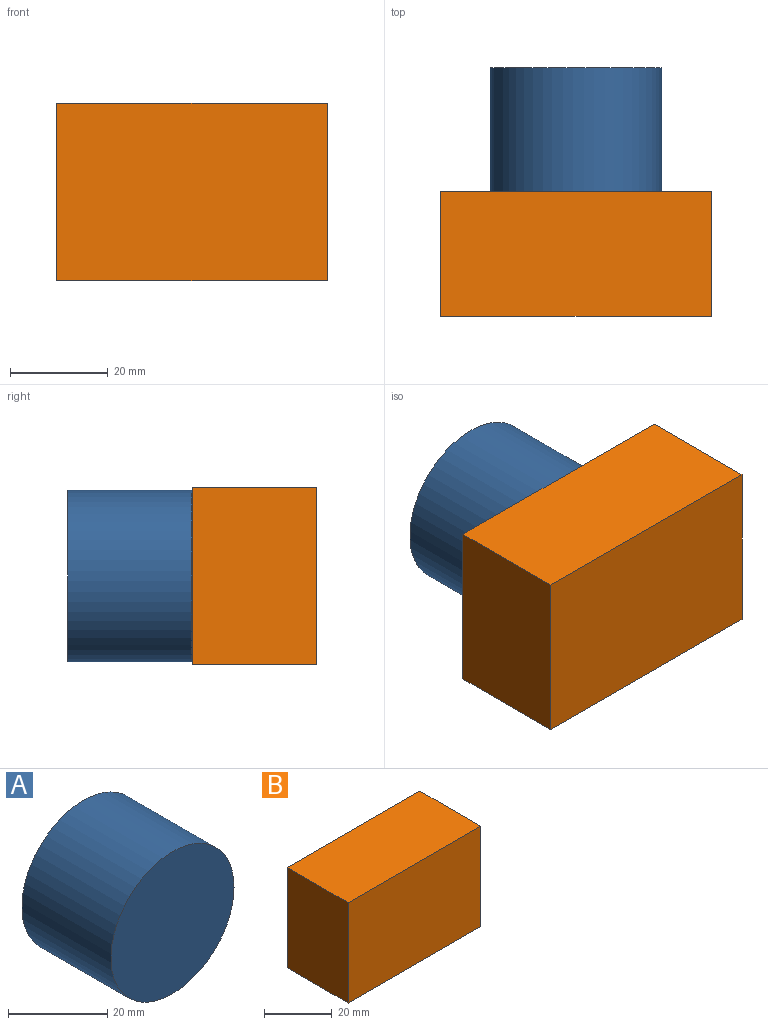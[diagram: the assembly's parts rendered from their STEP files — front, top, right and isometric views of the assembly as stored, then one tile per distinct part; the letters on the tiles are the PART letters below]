
ASSEMBLY  parts=2 mates=1
PART A: 3 faces, bbox 35.1x25.4x35.1 mm
  f0: cylinder r=17.55mm len=35.1mm, axis (0,1,0), area 2801mm2, adj f1,f2
  f1: plane 35.1x35.1mm, normal (0,-1,0), area 967.8mm2, adj f0
  f2: plane 35.1x35.1mm, normal (0,1,0), area 967.8mm2, adj f0
PART B: 6 faces, bbox 55.2x25.4x36.2 mm
  f0: plane 36.17x25.4mm, normal (-1,0,0), area 918.8mm2, adj f1,f3,f4,f5
  f1: plane 55.25x25.4mm, normal (0,0,-1), area 1403.3mm2, adj f0,f2,f4,f5
  f2: plane 36.17x25.4mm, normal (1,0,0), area 918.8mm2, adj f1,f3,f4,f5
  f3: plane 55.25x25.4mm, normal (0,0,1), area 1403.3mm2, adj f0,f2,f4,f5
  f4: plane 55.25x36.17mm, normal (0,-1,0), area 1998.5mm2, adj f0,f1,f2,f3
  f5: plane 55.25x36.17mm, normal (0,1,0), area 1998.5mm2, adj f0,f1,f2,f3
PLACE A t=(-58.38,4.7,-26.76)mm
PLACE B rot(axis=(1,0,0),180deg) t=(37.43,-46.1,36.2)mm
MATE revolute B.f4 <-> A.f0  axis (0,1,0) through (-20.89,-20.7,6.09)mm
